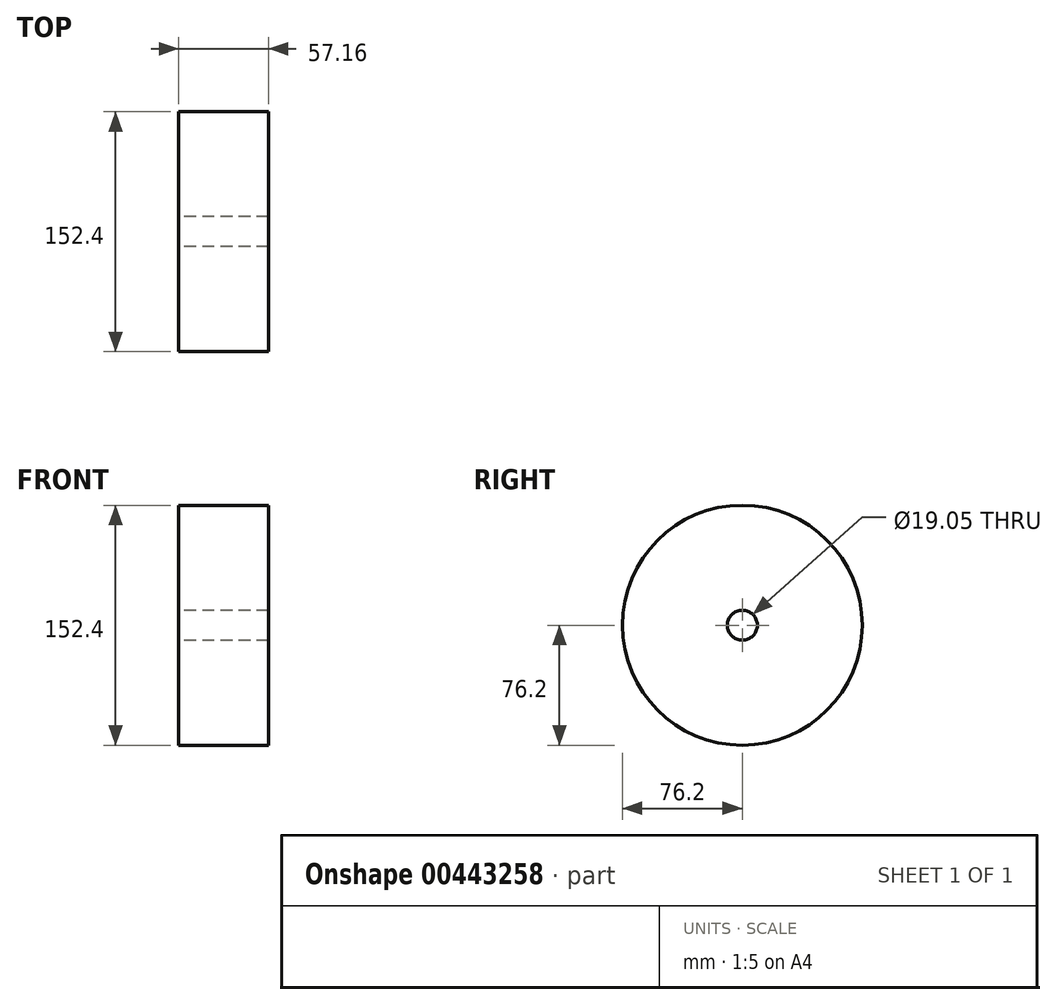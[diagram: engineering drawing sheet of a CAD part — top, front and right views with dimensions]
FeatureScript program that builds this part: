
annotation { "Feature Type Name" : "Feature", "Feature Type Description" : "" }
export const myFeature = defineFeature(function(context is Context, id is Id, definition is map)
    precondition{}
    {
        {
            var Q0;
            Q0=qCreatedBy(makeId("Right.planeOp"),FACE);
            var sketch = newSketch(context, id + "F0", { "sketchPlane" : qUnion([Q0])});
            skCircle(sketch, "E0", {"center": v(0, 0) * mm, "radius": 76.2 * mm});
            skCircle(sketch, "E1", {"center": v(0, 0) * mm, "radius": 9.53 * mm});
            skSolve(sketch);
        }
        {
            var Q0;
            Q0=makeQuery(id+"F0.imprint","IMPRINT",FACE,{"disambiguationData":[TD([[makeQuery(id+"F0.imprint","IMPRINT",EDGE,{"derivedFrom":sQuery(id+"F0.wireOp",EDGE,"E0")}),1.0]])]});
            extrude(context, id + "F1", {"entities" : qUnion([Q0]), "depth" : 57.15 * mm, "symmetric" : true});
        }
    });
